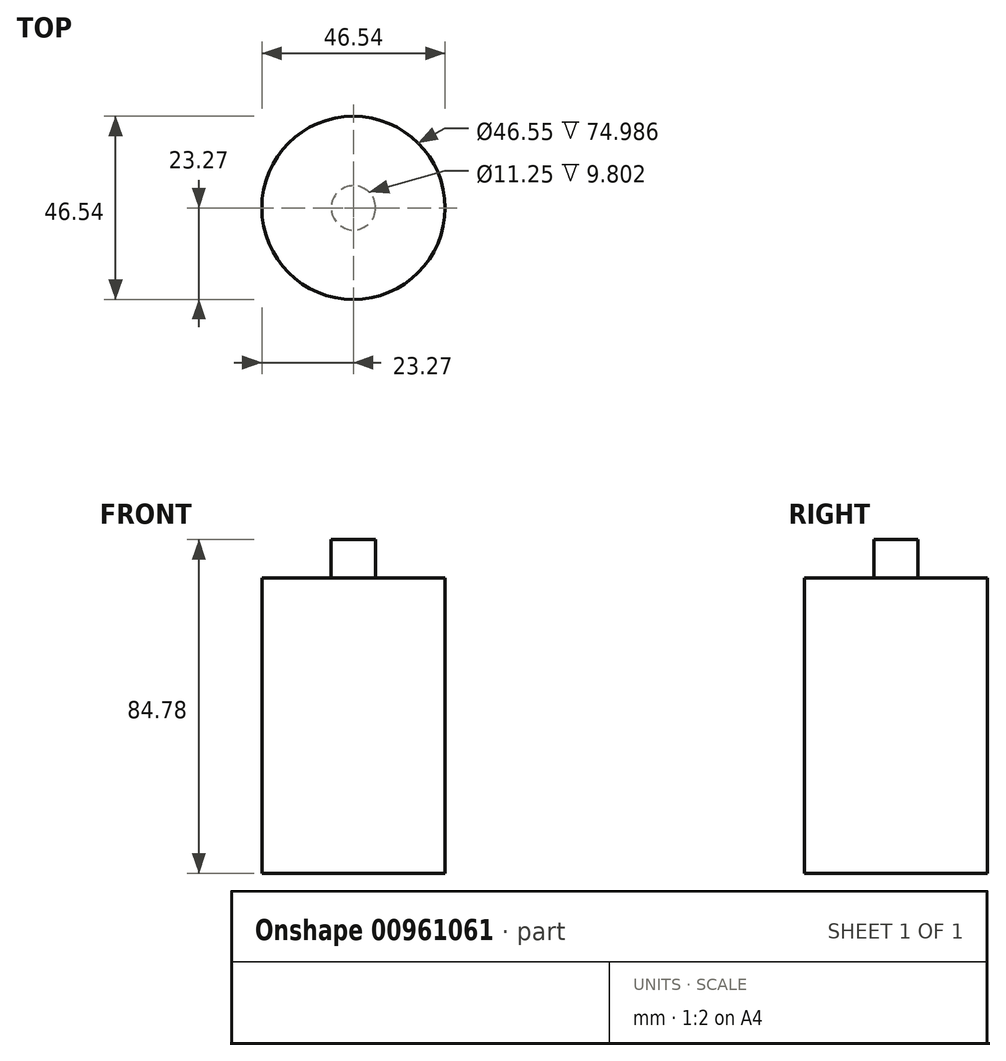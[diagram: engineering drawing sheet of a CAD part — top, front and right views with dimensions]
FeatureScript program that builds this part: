
annotation { "Feature Type Name" : "Feature", "Feature Type Description" : "" }
export const myFeature = defineFeature(function(context is Context, id is Id, definition is map)
    precondition{}
    {
        {
            var Q0;
            Q0=qCreatedBy(makeId("Front.planeOp"),FACE);
            var sketch = newSketch(context, id + "F0", { "sketchPlane" : qUnion([Q0])});
            skLineSegment(sketch, "E0", {"start": v(0, 44.6) * mm, "end": v(0, -44.84) * mm, "construction": true});
            skLineSegment(sketch, "E1", {"start": v(0, 39.94) * mm, "end": v(5.62, 39.94) * mm});
            skLineSegment(sketch, "E2", {"start": v(5.62, 39.94) * mm, "end": v(5.62, 30.14) * mm});
            skLineSegment(sketch, "E3", {"start": v(5.62, 30.14) * mm, "end": v(23.27, 30.14) * mm});
            skLineSegment(sketch, "E4", {"start": v(23.27, 30.14) * mm, "end": v(23.27, -44.84) * mm});
            skLineSegment(sketch, "E5", {"start": v(23.27, -44.84) * mm, "end": v(0, -44.84) * mm});
            skLineSegment(sketch, "E6.0", {"start": v(20.73, -42.3) * mm, "end": v(0, -42.3) * mm});
            skLineSegment(sketch, "E6.1", {"start": v(0, 37.4) * mm, "end": v(3.08, 37.4) * mm});
            skLineSegment(sketch, "E6.2", {"start": v(3.08, 37.4) * mm, "end": v(3.08, 27.6) * mm});
            skLineSegment(sketch, "E6.3", {"start": v(3.08, 27.6) * mm, "end": v(20.73, 27.6) * mm});
            skLineSegment(sketch, "E6.4", {"start": v(20.73, 27.6) * mm, "end": v(20.73, -42.3) * mm});
            skSolve(sketch);
        }
        {
            var Q0;
            Q0=sQuery(id+"F0.wireOp",EDGE,"E1");
            var Q1;
            Q1=sQuery(id+"F0.wireOp",EDGE,"E3");
            var Q2;
            Q2=sQuery(id+"F0.wireOp",EDGE,"E4");
            var Q3;
            Q3=sQuery(id+"F0.wireOp",EDGE,"E5");
            var Q4;
            Q4=sQuery(id+"F0.wireOp",EDGE,"E2");
            var Q5;
            Q5=sQuery(id+"F0.wireOp",EDGE,"E0");
            revolve(context, id + "F1", {"bodyType" : ToolBodyType.SURFACE, "surfaceOperationType" : NewSurfaceOperationType.NEW, "surfaceEntities" : qUnion([Q0, Q1, Q2, Q3, Q4]), "axis" : qUnion([Q5]), "revolveType" : RevolveType.FULL});
        }
    });
